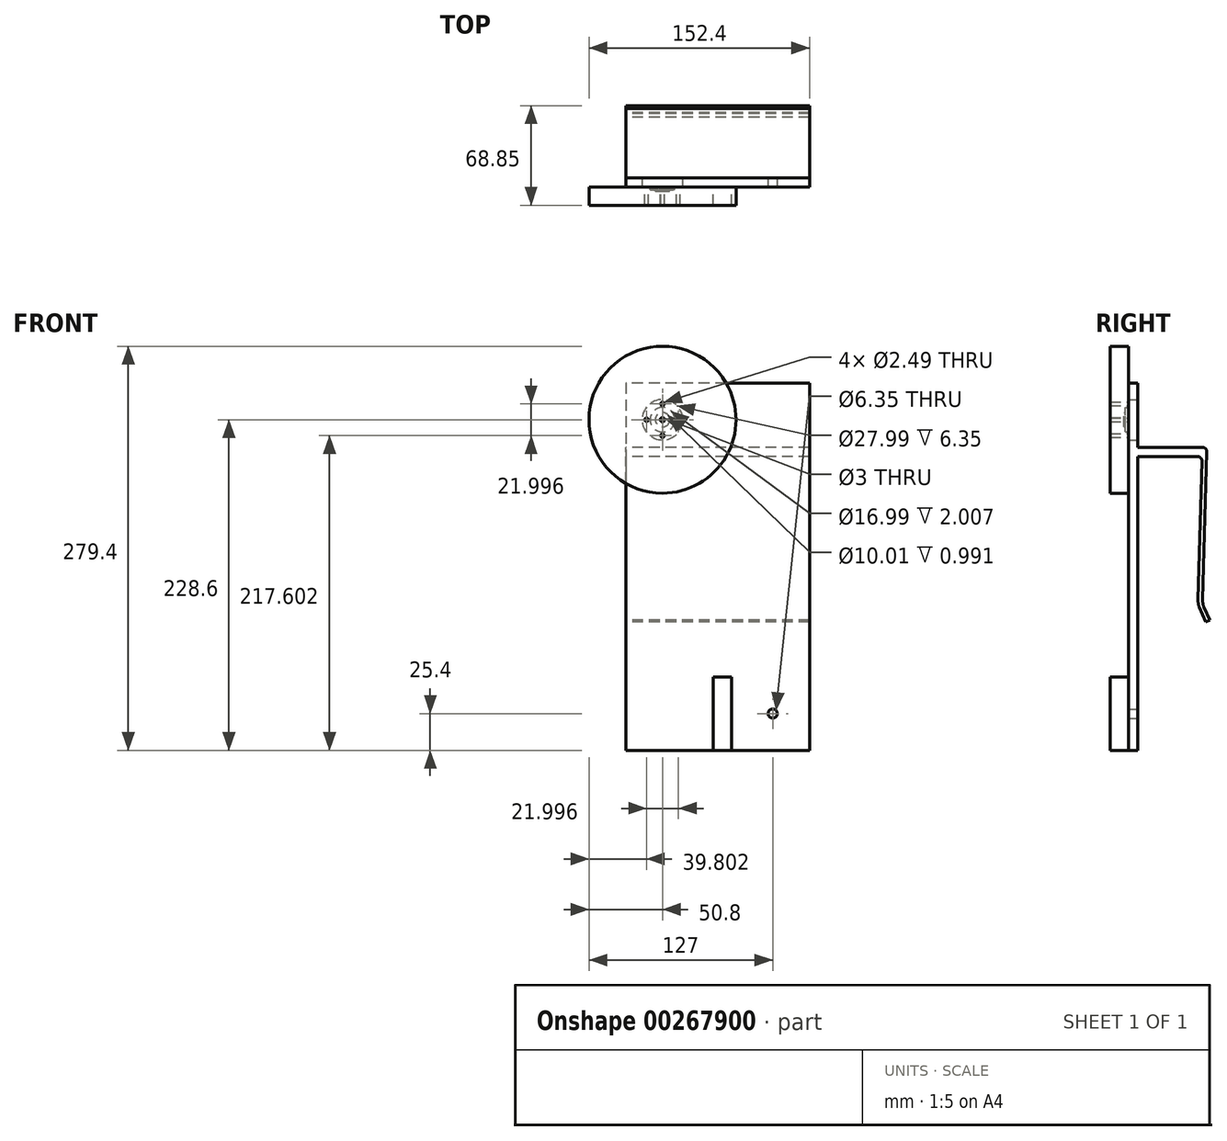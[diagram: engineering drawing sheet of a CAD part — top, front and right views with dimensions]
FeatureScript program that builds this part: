
annotation { "Feature Type Name" : "Feature", "Feature Type Description" : "" }
export const myFeature = defineFeature(function(context is Context, id is Id, definition is map)
    precondition{}
    {
        {
            var Q0;
            Q0=qCreatedBy(makeId("Front.planeOp"),FACE);
            var sketch = newSketch(context, id + "F0", { "sketchPlane" : qUnion([Q0])});
            skLineSegment(sketch, "E0.bottom", {"start": v(38.1, 101.6) * mm, "end": v(-38.1, 101.6) * mm, "construction": true});
            skLineSegment(sketch, "E0.top", {"start": v(38.1, -101.6) * mm, "end": v(-38.1, -101.6) * mm, "construction": true});
            skLineSegment(sketch, "E0.left", {"start": v(38.1, 101.6) * mm, "end": v(38.1, -101.6) * mm, "construction": true});
            skLineSegment(sketch, "E0.right", {"start": v(-38.1, 101.6) * mm, "end": v(-38.1, -101.6) * mm, "construction": true});
            skPoint(sketch, "E0.middle", {"position": v(0, 0) * mm});
            skCircle(sketch, "E1", {"center": v(38.1, 101.6) * mm, "radius": 3.18 * mm});
            skCircle(sketch, "E2", {"center": v(-38.1, -101.6) * mm, "radius": 3.18 * mm});
            skCircle(sketch, "E3", {"center": v(38.1, -101.6) * mm, "radius": 3.18 * mm});
            skLineSegment(sketch, "E4.bottom", {"start": v(63.5, 127) * mm, "end": v(-63.5, 127) * mm});
            skLineSegment(sketch, "E4.top", {"start": v(63.5, -127) * mm, "end": v(-63.5, -127) * mm});
            skLineSegment(sketch, "E4.left", {"start": v(63.5, 127) * mm, "end": v(63.5, -127) * mm});
            skLineSegment(sketch, "E4.right", {"start": v(-63.5, 127) * mm, "end": v(-63.5, -127) * mm});
            skCircle(sketch, "E5", {"center": v(-38.1, 101.6) * mm, "radius": 14 * mm});
            skSolve(sketch);
        }
        {
            var Q0;
            Q0=makeQuery(id+"F0.imprint","IMPRINT",FACE,{"disambiguationData":[TD([[makeQuery(id+"F0.imprint","IMPRINT",EDGE,{"derivedFrom":sQuery(id+"F0.wireOp",EDGE,"E1")}),-1.0]])]});
            var Q1;
            Q1=makeQuery(id+"F0.imprint","IMPRINT",FACE,{"disambiguationData":[TD([[makeQuery(id+"F0.imprint","IMPRINT",EDGE,{"derivedFrom":sQuery(id+"F0.wireOp",EDGE,"E1")}),1.0]])]});
            var Q2;
            Q2=makeQuery(id+"F0.imprint","IMPRINT",FACE,{"disambiguationData":[TD([[makeQuery(id+"F0.imprint","IMPRINT",EDGE,{"derivedFrom":sQuery(id+"F0.wireOp",EDGE,"E2")}),1.0]])]});
            extrude(context, id + "F1", {"entities" : qUnion([Q0, Q1, Q2]), "depth" : 6.35 * mm});
        }
        {
            var Q0;
            Q0=qCreatedBy(makeId("Right.planeOp"),FACE);
            var sketch = newSketch(context, id + "F2", { "sketchPlane" : qUnion([Q0])});
            skLineSegment(sketch, "E6", {"start": v(0, 82.55) * mm, "end": v(44.64, 82.55) * mm});
            skLineSegment(sketch, "E7", {"start": v(47.81, 79.28) * mm, "end": v(44.84, -22.55) * mm});
            skLineSegment(sketch, "E8", {"start": v(45.9, -28.01) * mm, "end": v(49.8, -36.93) * mm});
            skLineSegment(sketch, "E9", {"start": v(49.8, -36.93) * mm, "end": v(47.13, -38.1) * mm});
            skLineSegment(sketch, "E10", {"start": v(47.13, -38.1) * mm, "end": v(42.72, -28.01) * mm});
            skLineSegment(sketch, "E11", {"start": v(41.66, -22.55) * mm, "end": v(44.45, 72.93) * mm});
            skLineSegment(sketch, "E12", {"start": v(41.28, 76.2) * mm, "end": v(0, 76.2) * mm});
            skLineSegment(sketch, "E13", {"start": v(0, 82.55) * mm, "end": v(0, 76.2) * mm});
            skPoint(sketch, "E14.visualSharp", {"position": v(44.55, 76.2) * mm});
            skArc(sketch, "E14.filletArc", {"start": v(44.45, 72.93) * mm, "mid": v(43.55, 75.24) * mm, "end": v(41.28, 76.2) * mm});
            skPoint(sketch, "E15.visualSharp", {"position": v(47.9, 82.55) * mm});
            skArc(sketch, "E15.filletArc", {"start": v(47.81, 79.28) * mm, "mid": v(46.92, 81.59) * mm, "end": v(44.64, 82.55) * mm});
            skPoint(sketch, "E16.visualSharp", {"position": v(41.58, -25.4) * mm});
            skArc(sketch, "E16.filletArc", {"start": v(41.66, -22.55) * mm, "mid": v(41.89, -25.34) * mm, "end": v(42.72, -28.01) * mm});
            skPoint(sketch, "E17.visualSharp", {"position": v(44.75, -25.4) * mm});
            skArc(sketch, "E17.filletArc", {"start": v(44.84, -22.55) * mm, "mid": v(45.06, -25.34) * mm, "end": v(45.9, -28.01) * mm});
            skSolve(sketch);
        }
        {
            var Q0;
            Q0=makeQuery(id+"F2.imprint","IMPRINT",FACE,{"disambiguationData":[TD([[makeQuery(id+"F2.imprint","IMPRINT",EDGE,{"derivedFrom":sQuery(id+"F2.wireOp",EDGE,"E6")}),-1.0]])]});
            var Q1;
            Q1=makeQuery(id+"F1.opExtrude","SWEPT_FACE",FACE,{"disambiguationData":[OSD([sQuery(id+"F0.wireOp",EDGE,"E4.left")])]});
            extrude(context, id + "F3", {"entities" : qUnion([Q0]), "operationType" : NewBodyOperationType.ADD, "endBound" : BoundingType.SYMMETRIC, "endBoundEntityFace" : qUnion([Q1]), "depth" : 127 * mm});
        }
        {
            var Q0;
            Q0=makeQuery(id+"F1.opExtrude","CAP_FACE",FACE,{"disambiguationData":[OSD([sQuery(id+"F0.wireOp",EDGE,"E3"),sQuery(id+"F0.wireOp",EDGE,"E4.bottom"),sQuery(id+"F0.wireOp",EDGE,"E4.top"),sQuery(id+"F0.wireOp",EDGE,"E4.left"),sQuery(id+"F0.wireOp",EDGE,"E4.right"),sQuery(id+"F0.wireOp",EDGE,"E5")])],"isStart":false});
            var sketch = newSketch(context, id + "F4", { "sketchPlane" : qUnion([Q0])});
            skLineSegment(sketch, "E18", {"start": v(-63.5, 73.2) * mm, "end": v(-63.5, 57.6) * mm});
            skCircle(sketch, "E19", {"center": v(-38.1, 101.6) * mm, "radius": 50.8 * mm});
            skCircle(sketch, "E20.0", {"center": v(-38.1, 101.6) * mm, "radius": 14 * mm});
            skCircle(sketch, "E21", {"center": v(-38.1, 101.6) * mm, "radius": 8.5 * mm});
            skCircle(sketch, "E22", {"center": v(-38.1, 101.6) * mm, "radius": 1.5 * mm});
            skCircle(sketch, "E23", {"center": v(-38.1, 101.6) * mm, "radius": 5 * mm});
            skLineSegment(sketch, "E24", {"start": v(-49.1, 101.6) * mm, "end": v(-27.1, 101.6) * mm, "construction": true});
            skLineSegment(sketch, "E25", {"start": v(-38.1, 112.6) * mm, "end": v(-38.1, 90.6) * mm, "construction": true});
            skCircle(sketch, "E26", {"center": v(-38.1, 112.6) * mm, "radius": 1.24 * mm});
            skCircle(sketch, "E27", {"center": v(-27.1, 101.6) * mm, "radius": 1.24 * mm});
            skCircle(sketch, "E28", {"center": v(-38.1, 90.6) * mm, "radius": 1.24 * mm});
            skCircle(sketch, "E29", {"center": v(-49.1, 101.6) * mm, "radius": 1.24 * mm});
            skLineSegment(sketch, "E30.bottom", {"start": v(-3.17, -127) * mm, "end": v(9.53, -127) * mm});
            skLineSegment(sketch, "E30.top", {"start": v(-3.17, -76.2) * mm, "end": v(9.53, -76.2) * mm});
            skLineSegment(sketch, "E30.left", {"start": v(-3.17, -127) * mm, "end": v(-3.17, -76.2) * mm});
            skLineSegment(sketch, "E30.right", {"start": v(9.53, -127) * mm, "end": v(9.53, -76.2) * mm});
            skSolve(sketch);
        }
        {
            var Q0;
            {var subQ0=sQuery(id+"F4.wireOp",EDGE,"E18");Q0=makeQuery(id+"F4.imprint","IMPRINT",FACE,{"disambiguationData":[TD([[makeQuery(id+"F4.imprint","IMPRINT",EDGE,{"derivedFrom":subQ0}),-1.0]])]});}
            var Q1;
            {var subQ5=sQuery(id+"F4.wireOp",EDGE,"E18");Q1=makeQuery(id+"F4.imprint","IMPRINT",FACE,{"disambiguationData":[TD([[makeQuery(id+"F4.imprint","IMPRINT",EDGE,{"derivedFrom":subQ5}),1.0]])]});}
            var Q2;
            Q2=makeQuery(id+"F4.imprint","IMPRINT",FACE,{"disambiguationData":[TD([[makeQuery(id+"F4.imprint","IMPRINT",EDGE,{"derivedFrom":sQuery(id+"F4.wireOp",EDGE,"E20.0")}),1.0]])]});
            var Q3;
            Q3=makeQuery(id+"F4.imprint","IMPRINT",FACE,{"disambiguationData":[TD([[makeQuery(id+"F4.imprint","IMPRINT",EDGE,{"derivedFrom":sQuery(id+"F4.wireOp",EDGE,"E21")}),1.0]])]});
            var Q4;
            Q4=makeQuery(id+"F4.imprint","IMPRINT",FACE,{"disambiguationData":[TD([[makeQuery(id+"F4.imprint","IMPRINT",EDGE,{"derivedFrom":sQuery(id+"F4.wireOp",EDGE,"E22")}),-1.0]])]});
            var Q5;
            Q5=makeQuery(id+"F4.imprint","IMPRINT",FACE,{"disambiguationData":[TD([[makeQuery(id+"F4.imprint","IMPRINT",EDGE,{"derivedFrom":sQuery(id+"F4.wireOp",EDGE,"E30.bottom")}),-1.0]])]});
            extrude(context, id + "F5", {"entities" : qUnion([Q0, Q1, Q2, Q3, Q4, Q5]), "operationType" : NewBodyOperationType.ADD, "depth" : 12.7 * mm});
        }
        {
            var Q0;
            Q0=makeQuery(id+"F4.imprint","IMPRINT",FACE,{"disambiguationData":[TD([[makeQuery(id+"F4.imprint","IMPRINT",EDGE,{"derivedFrom":sQuery(id+"F4.wireOp",EDGE,"E21")}),1.0]])]});
            var Q1;
            Q1=makeQuery(id+"F4.imprint","IMPRINT",FACE,{"disambiguationData":[TD([[makeQuery(id+"F4.imprint","IMPRINT",EDGE,{"derivedFrom":sQuery(id+"F4.wireOp",EDGE,"E22")}),-1.0]])]});
            extrude(context, id + "F6", {"entities" : qUnion([Q0, Q1]), "operationType" : NewBodyOperationType.REMOVE, "depth" : 2 * mm});
        }
        {
            var Q0;
            Q0=makeQuery(id+"F4.imprint","IMPRINT",FACE,{"disambiguationData":[TD([[makeQuery(id+"F4.imprint","IMPRINT",EDGE,{"derivedFrom":sQuery(id+"F4.wireOp",EDGE,"E22")}),-1.0]])]});
            extrude(context, id + "F7", {"entities" : qUnion([Q0]), "operationType" : NewBodyOperationType.REMOVE, "depth" : 3 * mm});
        }
    });
